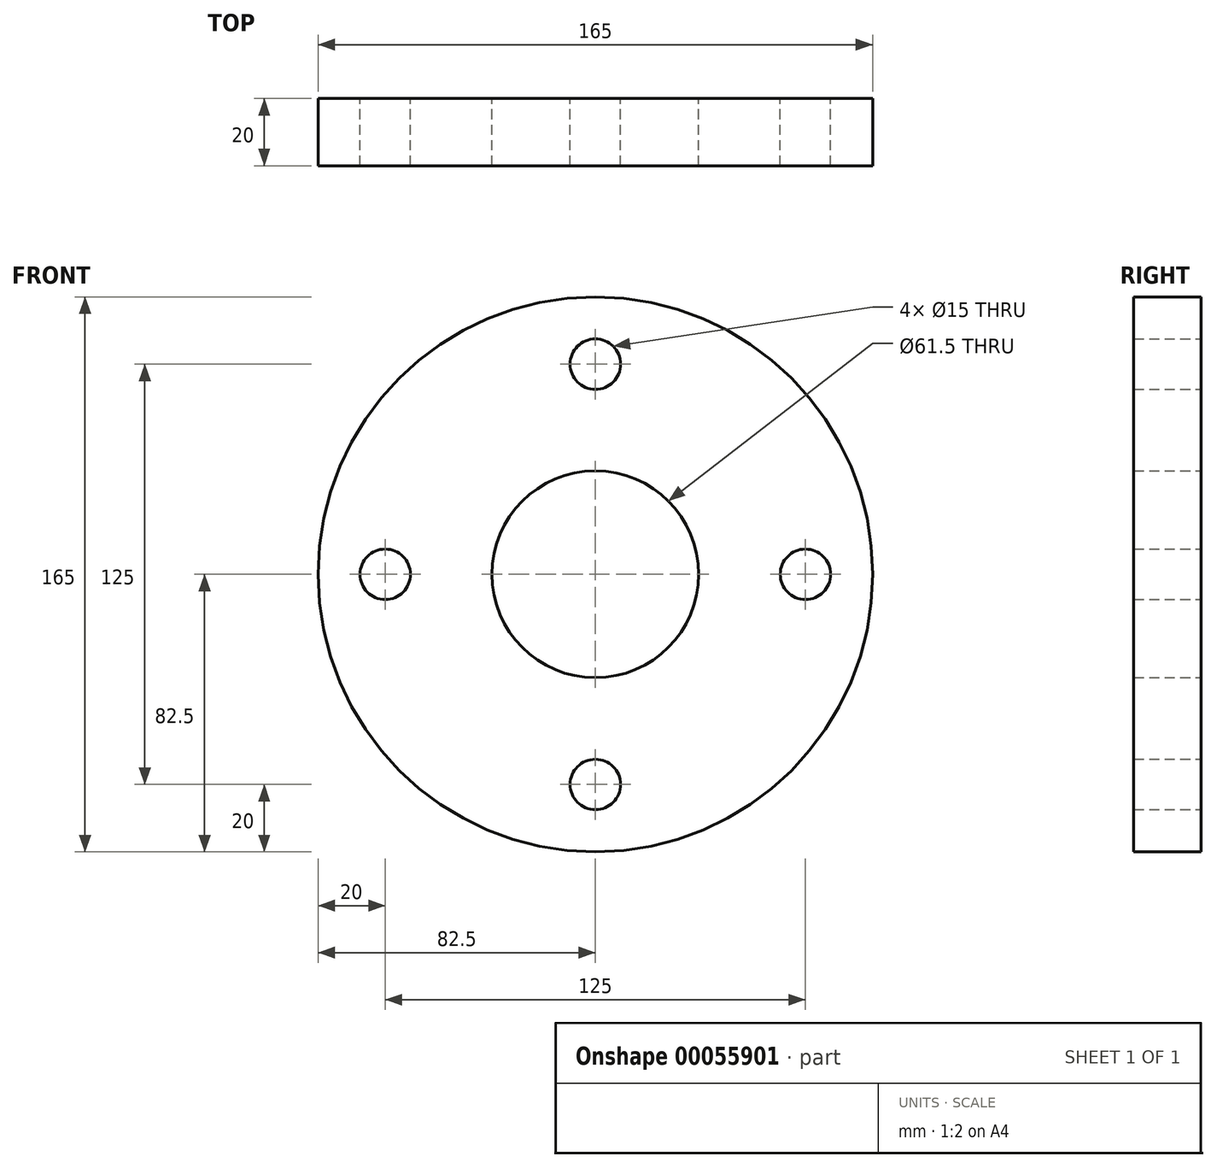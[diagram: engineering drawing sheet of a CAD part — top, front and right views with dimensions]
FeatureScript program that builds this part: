
annotation { "Feature Type Name" : "Feature", "Feature Type Description" : "" }
export const myFeature = defineFeature(function(context is Context, id is Id, definition is map)
    precondition{}
    {
        {
            var Q0;
            Q0=qCreatedBy(makeId("Front.planeOp"),FACE);
            var sketch = newSketch(context, id + "F0", { "sketchPlane" : qUnion([Q0])});
            skCircle(sketch, "E0", {"center": v(0, 0) * mm, "radius": 30.75 * mm});
            skCircle(sketch, "E1", {"center": v(0, 0) * mm, "radius": 82.5 * mm});
            skCircle(sketch, "E2", {"center": v(0, 0) * mm, "radius": 62.5 * mm, "construction": true});
            skSolve(sketch);
        }
        {
            var Q0;
            Q0=makeQuery(id+"F0.imprint","IMPRINT",FACE,{"disambiguationData":[TD([[makeQuery(id+"F0.imprint","IMPRINT",EDGE,{"derivedFrom":sQuery(id+"F0.wireOp",EDGE,"E0")}),-1.0]])]});
            extrude(context, id + "F1", {"entities" : qUnion([Q0]), "depth" : 20 * mm});
        }
        {
            var Q0;
            Q0=makeQuery(id+"F1.opExtrude","CAP_FACE",FACE,{"disambiguationData":[OSD([sQuery(id+"F0.wireOp",EDGE,"E0"),sQuery(id+"F0.wireOp",EDGE,"E1")])],"isStart":true});
            var sketch = newSketch(context, id + "F2", { "sketchPlane" : qUnion([Q0])});
            skCircle(sketch, "E3", {"center": v(0, 0) * mm, "radius": 62.5 * mm, "construction": true});
            skCircle(sketch, "E4", {"center": v(-62.5, 0) * mm, "radius": 7.5 * mm});
            skCircle(sketch, "E5.1.0", {"center": v(0, -62.5) * mm, "radius": 7.5 * mm});
            skCircle(sketch, "E5.2.0", {"center": v(62.5, 0) * mm, "radius": 7.5 * mm});
            skCircle(sketch, "E5.3.0", {"center": v(0, 62.5) * mm, "radius": 7.5 * mm});
            skSolve(sketch);
        }
        {
            var Q0;
            Q0=makeQuery(id+"F2.imprint","IMPRINT",FACE,{"disambiguationData":[TD([[makeQuery(id+"F2.imprint","IMPRINT",EDGE,{"derivedFrom":sQuery(id+"F2.wireOp",EDGE,"E5.1.0")}),1.0]])]});
            var Q1;
            Q1=makeQuery(id+"F2.imprint","IMPRINT",FACE,{"disambiguationData":[TD([[makeQuery(id+"F2.imprint","IMPRINT",EDGE,{"derivedFrom":sQuery(id+"F2.wireOp",EDGE,"E5.2.0")}),1.0]])]});
            var Q2;
            Q2=makeQuery(id+"F2.imprint","IMPRINT",FACE,{"disambiguationData":[TD([[makeQuery(id+"F2.imprint","IMPRINT",EDGE,{"derivedFrom":sQuery(id+"F2.wireOp",EDGE,"E5.3.0")}),1.0]])]});
            var Q3;
            Q3=makeQuery(id+"F2.imprint","IMPRINT",FACE,{"disambiguationData":[TD([[makeQuery(id+"F2.imprint","IMPRINT",EDGE,{"derivedFrom":sQuery(id+"F2.wireOp",EDGE,"E4")}),1.0]])]});
            extrude(context, id + "F3", {"entities" : qUnion([Q0, Q1, Q2, Q3]), "operationType" : NewBodyOperationType.REMOVE, "endBound" : BoundingType.THROUGH_ALL, "oppositeDirection" : true, "depth" : 25 * mm});
        }
    });
